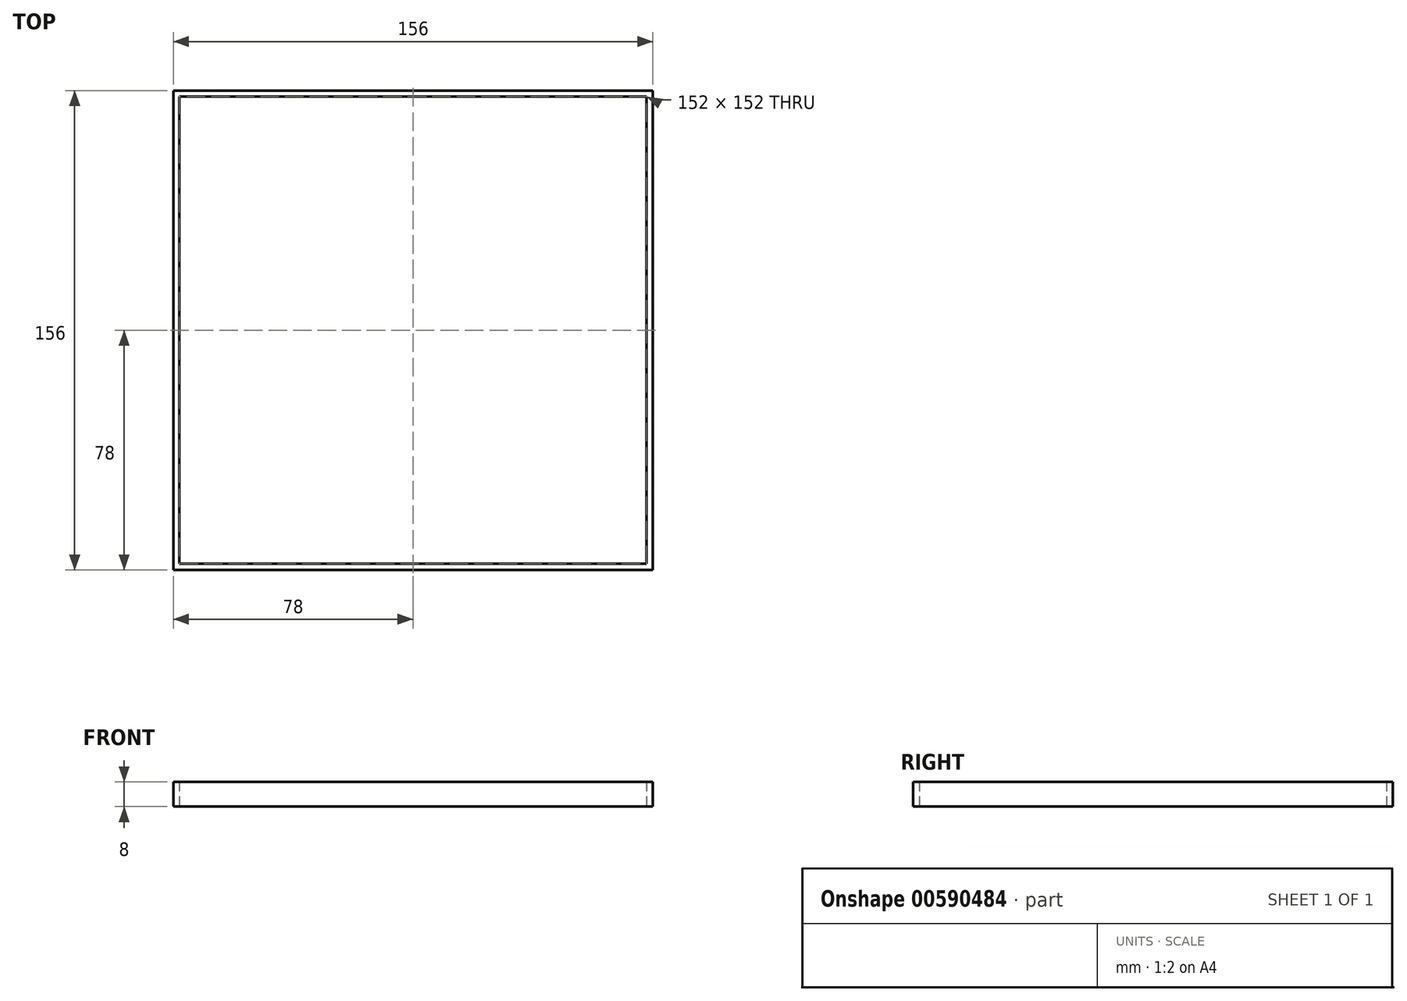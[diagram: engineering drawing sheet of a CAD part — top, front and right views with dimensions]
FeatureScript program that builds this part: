
annotation { "Feature Type Name" : "Feature", "Feature Type Description" : "" }
export const myFeature = defineFeature(function(context is Context, id is Id, definition is map)
    precondition{}
    {
        {
            var Q0;
            Q0=qCreatedBy(makeId("Top.planeOp"),FACE);
            var sketch = newSketch(context, id + "F0", { "sketchPlane" : qUnion([Q0])});
            skLineSegment(sketch, "E0.bottom", {"start": v(76, 76) * mm, "end": v(-76, 76) * mm});
            skLineSegment(sketch, "E0.top", {"start": v(76, -76) * mm, "end": v(-76, -76) * mm});
            skLineSegment(sketch, "E0.left", {"start": v(76, 76) * mm, "end": v(76, -76) * mm});
            skLineSegment(sketch, "E0.right", {"start": v(-76, 76) * mm, "end": v(-76, -76) * mm});
            skPoint(sketch, "E0.middle", {"position": v(0, 0) * mm});
            skLineSegment(sketch, "E1.0", {"start": v(78, -78) * mm, "end": v(-78, -78) * mm});
            skLineSegment(sketch, "E1.1", {"start": v(78, 78) * mm, "end": v(78, -78) * mm});
            skLineSegment(sketch, "E1.2", {"start": v(78, 78) * mm, "end": v(-78, 78) * mm});
            skLineSegment(sketch, "E1.3", {"start": v(-78, 78) * mm, "end": v(-78, -78) * mm});
            skSolve(sketch);
        }
        {
            var Q0;
            Q0=makeQuery(id+"F0.imprint","IMPRINT",FACE,{"disambiguationData":[TD([[makeQuery(id+"F0.imprint","IMPRINT",EDGE,{"derivedFrom":sQuery(id+"F0.wireOp",EDGE,"E0.bottom")}),-1.0]])]});
            extrude(context, id + "F1", {"entities" : qUnion([Q0]), "depth" : 8 * mm, "offsetDistance" : 25 * mm});
        }
    });
